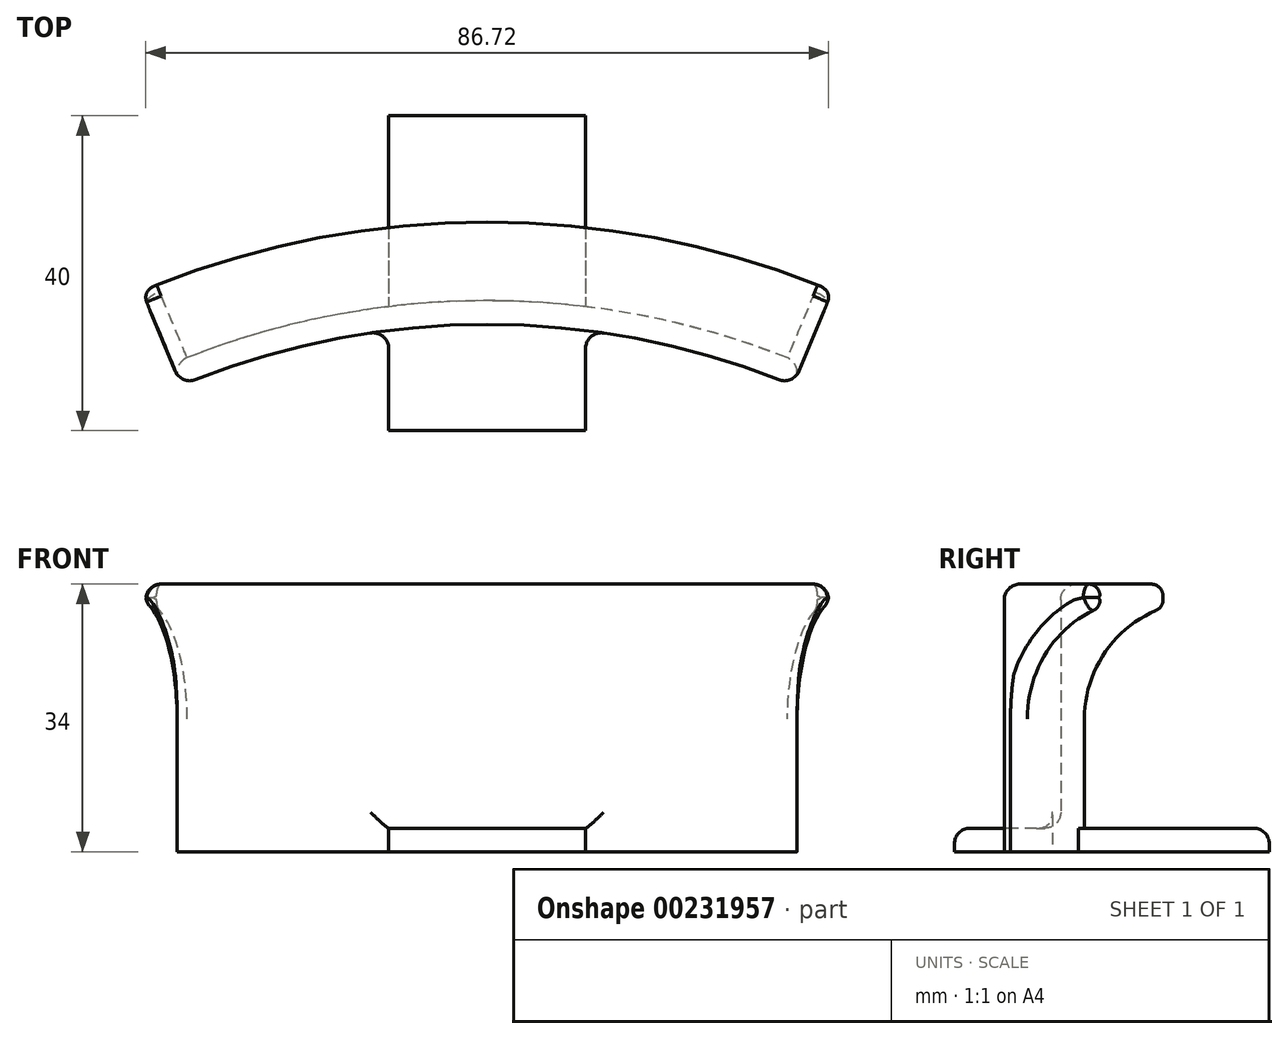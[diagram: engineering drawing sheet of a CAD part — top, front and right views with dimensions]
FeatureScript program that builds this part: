
annotation { "Feature Type Name" : "Feature", "Feature Type Description" : "" }
export const myFeature = defineFeature(function(context is Context, id is Id, definition is map)
    precondition{}
    {
        {
            var Q0;
            Q0=qCreatedBy(makeId("Top.planeOp"),FACE);
            var sketch = newSketch(context, id + "F0", { "sketchPlane" : qUnion([Q0])});
            skArc(sketch, "E0", {"start": v(40, 0) * mm, "mid": v(0, 8) * mm, "end": v(-40, 0) * mm});
            skPoint(sketch, "E1", {"position": v(0, 8) * mm});
            skArc(sketch, "E2.0", {"start": v(38.85, -2.77) * mm, "mid": v(0, 5) * mm, "end": v(-38.85, -2.77) * mm});
            skLineSegment(sketch, "E3", {"start": v(-40, 0) * mm, "end": v(-38.85, -2.77) * mm});
            skLineSegment(sketch, "E4", {"start": v(40, 0) * mm, "end": v(38.85, -2.77) * mm});
            skSolve(sketch);
        }
        {
            var Q0;
            Q0=qSketchRegion(id+"F0",true);
            var Q1;
            Q1 = qSketchRegion(id + "F2", true);
            extrude(context, id + "F1", {"entities" : qUnion([Q0, Q1]), "endBound" : BoundingType.SYMMETRIC, "depth" : 34 * mm, "hasSecondDirection" : true, "secondDirectionOppositeDirection" : true, "secondDirectionDepth" : 25 * mm});
        }
        {
            var Q0;
            Q0=makeQuery(id+"F1.opExtrude","CAP_FACE",FACE,{"disambiguationData":[OSD([sQuery(id+"F0.wireOp",EDGE,"E0"),sQuery(id+"F0.wireOp",EDGE,"E2.0"),sQuery(id+"F0.wireOp",EDGE,"E3"),sQuery(id+"F0.wireOp",EDGE,"E4"),sQuery(id+"F0.wireOp",EDGE,"MKCCxzGF-fzHT-6NQb-3Dkm-oyMVu23sNnWI"),sQuery(id+"F0.wireOp",EDGE,"RX4jBwC5-T415-0Oy0-ZdqJ-OYdbBSf1K6n9"),sQuery(id+"F0.wireOp",EDGE,"Lq5RhwRJ-kZL3-UkZd-qRQH-dxPEWorBv0Qx"),sQuery(id+"F0.wireOp",EDGE,"eGbxxHlE-VtXz-Rjba-jT0Z-kXdZI8RM2eGt"),sQuery(id+"F0.wireOp",EDGE,"FihKfQdN-VEdl-hHsK-2V6z-z5lvR1BBxPRn"),sQuery(id+"F0.wireOp",EDGE,"HknWR3fc-V9o8-nyJb-E4uW-t3jdVaxvh762"),sQuery(id+"F0.wireOp",EDGE,"368abe3e-c0fb-4884-afcf-caa45f78abb90.MirrorCS"),sQuery(id+"F0.wireOp",EDGE,"368abe3e-c0fb-4884-afcf-caa45f78abb91.MirrorCS"),sQuery(id+"F0.wireOp",EDGE,"368abe3e-c0fb-4884-afcf-caa45f78abb92.MirrorCS"),sQuery(id+"F0.wireOp",EDGE,"368abe3e-c0fb-4884-afcf-caa45f78abb93.MirrorCS"),sQuery(id+"F0.wireOp",EDGE,"368abe3e-c0fb-4884-afcf-caa45f78abb94.MirrorCS")])],"isStart":false});
            var sketch = newSketch(context, id + "F2", { "sketchPlane" : qUnion([Q0])});
            skArc(sketch, "E5", {"start": v(38.85, -2.77) * mm, "mid": v(0, 5) * mm, "end": v(-38.85, -2.77) * mm});
            skArc(sketch, "E6.0", {"start": v(43.85, 9.23) * mm, "mid": v(0, 18) * mm, "end": v(-43.85, 9.23) * mm});
            skLineSegment(sketch, "E7", {"start": v(-43.85, 9.23) * mm, "end": v(-38.85, -2.77) * mm});
            skLineSegment(sketch, "E8", {"start": v(43.85, 9.23) * mm, "end": v(38.85, -2.77) * mm});
            skSolve(sketch);
        }
        {
            var Q0;
            Q0=qSketchRegion(id+"F2",true);
            extrude(context, id + "F3", {"entities" : qUnion([Q0]), "operationType" : NewBodyOperationType.ADD, "oppositeDirection" : true, "depth" : 3 * mm});
        }
        {
            var Q0;
            Q0=makeQuery(id+"F3.boolean.opBoolean","INTERSECT",EDGE,{"derivedFrom":[makeQuery(id+"F1.opExtrude","SWEPT_FACE",FACE,{"disambiguationData":[OSD([sQuery(id+"F0.wireOp",EDGE,"E0")])]}),makeQuery(id+"F3.opExtrude","CAP_FACE",FACE,{"disambiguationData":[OSD([sQuery(id+"F2.wireOp",EDGE,"E5"),sQuery(id+"F2.wireOp",EDGE,"E6.0"),sQuery(id+"F2.wireOp",EDGE,"E7"),sQuery(id+"F2.wireOp",EDGE,"E8")])],"isStart":false})]});
            var Q1;
            Q1=makeQuery(id+"FpLEZJu2neVifi9_1.1.F3.boolean.opBoolean","INTERSECT",EDGE,{"derivedFrom":[makeQuery(id+"F1.opExtrude","SWEPT_FACE",FACE,{"disambiguationData":[OSD([sQuery(id+"F0.wireOp",EDGE,"E0")])]}),makeQuery(id+"FpLEZJu2neVifi9_1.1.F3.opExtrude","CAP_FACE",FACE,{"disambiguationData":[OSD([sQuery(id+"F2.wireOp",EDGE,"E5"),sQuery(id+"F2.wireOp",EDGE,"E6.0"),sQuery(id+"F2.wireOp",EDGE,"E7"),sQuery(id+"F2.wireOp",EDGE,"E8")])],"isStart":false})]});
            fillet(context, id + "F4", {"entities" : qUnion([Q0, Q1]), "radius" : 15 * mm, "tangentPropagation" : true, "allowEdgeOverflow" : false});
        }
        {
            var Q0;
            Q0=makeQuery(id+"FpLEZJu2neVifi9_1.1.F3.boolean.opBoolean","MERGE",FACE,{"derivedFrom":[makeQuery(id+"F1.opExtrude","CAP_FACE",FACE,{"disambiguationData":[OSD([sQuery(id+"F0.wireOp",EDGE,"E0"),sQuery(id+"F0.wireOp",EDGE,"E2.0"),sQuery(id+"F0.wireOp",EDGE,"E3"),sQuery(id+"F0.wireOp",EDGE,"E4")])],"isStart":true}),makeQuery(id+"FpLEZJu2neVifi9_1.1.F3.opExtrude","CAP_FACE",FACE,{"disambiguationData":[OSD([sQuery(id+"F2.wireOp",EDGE,"E5"),sQuery(id+"F2.wireOp",EDGE,"E6.0"),sQuery(id+"F2.wireOp",EDGE,"E7"),sQuery(id+"F2.wireOp",EDGE,"E8")])],"isStart":true})]});
            var sketch = newSketch(context, id + "F5", { "sketchPlane" : qUnion([Q0])});
            skLineSegment(sketch, "E9.bottom", {"start": v(12.5, -31.5) * mm, "end": v(-12.5, -31.5) * mm});
            skLineSegment(sketch, "E9.top", {"start": v(12.5, 8.5) * mm, "end": v(-12.5, 8.5) * mm});
            skLineSegment(sketch, "E9.left", {"start": v(12.5, -31.5) * mm, "end": v(12.5, 8.5) * mm});
            skLineSegment(sketch, "E9.right", {"start": v(-12.5, -31.5) * mm, "end": v(-12.5, 8.5) * mm});
            skLineSegment(sketch, "E10", {"start": v(0, -18) * mm, "end": v(0, -5) * mm, "construction": true});
            skPoint(sketch, "E11", {"position": v(0, -11.5) * mm});
            skLineSegment(sketch, "E12", {"start": v(12.5, -31.5) * mm, "end": v(-12.5, 8.5) * mm, "construction": true});
            skSolve(sketch);
        }
        {
            var Q0;
            Q0 = qSketchRegion(id + "F5", true);
            extrude(context, id + "F6", {"entities" : qUnion([Q0]), "operationType" : NewBodyOperationType.ADD, "oppositeDirection" : true, "depth" : 3 * mm});
        }
        {
            var Q0;
            Q0=makeQuery(id+"F6.boolean.opBoolean","INTERSECT",EDGE,{"derivedFrom":[makeQuery(id+"FpLEZJu2neVifi9_1.1.F3.opExtrude","SWEPT_FACE",FACE,{"disambiguationData":[OSD([sQuery(id+"F2.wireOp",EDGE,"E6.0")])]}),makeQuery(id+"F6.opExtrude","SWEPT_FACE",FACE,{"disambiguationData":[OSD([sQuery(id+"F5.wireOp",EDGE,"E9.left")])]})]});
            var Q1;
            Q1=makeQuery(id+"F6.boolean.opBoolean","INTERSECT",EDGE,{"derivedFrom":[makeQuery(id+"FpLEZJu2neVifi9_1.1.F3.opExtrude","SWEPT_FACE",FACE,{"disambiguationData":[OSD([sQuery(id+"F2.wireOp",EDGE,"E6.0")])]}),makeQuery(id+"F6.opExtrude","SWEPT_FACE",FACE,{"disambiguationData":[OSD([sQuery(id+"F5.wireOp",EDGE,"E9.right")])]})]});
            var Q2;
            Q2=makeQuery(id+"F6.boolean.opBoolean","INTERSECT",EDGE,{"derivedFrom":[makeQuery(id+"F1.opExtrude","SWEPT_FACE",FACE,{"disambiguationData":[OSD([sQuery(id+"F0.wireOp",EDGE,"E2.0")])]}),makeQuery(id+"F6.opExtrude","SWEPT_FACE",FACE,{"disambiguationData":[OSD([sQuery(id+"F5.wireOp",EDGE,"E9.left")])]})]});
            var Q3;
            Q3=makeQuery(id+"F6.boolean.opBoolean","INTERSECT",EDGE,{"derivedFrom":[makeQuery(id+"F1.opExtrude","SWEPT_FACE",FACE,{"disambiguationData":[OSD([sQuery(id+"F0.wireOp",EDGE,"E2.0")])]}),makeQuery(id+"F6.opExtrude","SWEPT_FACE",FACE,{"disambiguationData":[OSD([sQuery(id+"F5.wireOp",EDGE,"E9.right")])]})]});
            var Q4;
            {var subQ0=sQuery(id+"F2.wireOp",EDGE,"E7");Q4=makeQuery(id+"FpLEZJu2neVifi9_1.1.F3.boolean.opBoolean","MERGE",FACE,{"derivedFrom":[makeQuery(id+"F3.boolean.opBoolean","MERGE",FACE,{"derivedFrom":[makeQuery(id+"F1.opExtrude","SWEPT_FACE",FACE,{"disambiguationData":[OSD([sQuery(id+"F0.wireOp",EDGE,"E3")])]}),makeQuery(id+"F3.opExtrude","SWEPT_FACE",FACE,{"disambiguationData":[OSD([subQ0])]})]}),makeQuery(id+"FpLEZJu2neVifi9_1.1.F3.opExtrude","SWEPT_FACE",FACE,{"disambiguationData":[OSD([subQ0])]})]});}
            var Q5;
            {var subQ0=sQuery(id+"F2.wireOp",EDGE,"E8");Q5=makeQuery(id+"FpLEZJu2neVifi9_1.1.F3.boolean.opBoolean","MERGE",FACE,{"derivedFrom":[makeQuery(id+"F3.boolean.opBoolean","MERGE",FACE,{"derivedFrom":[makeQuery(id+"F1.opExtrude","SWEPT_FACE",FACE,{"disambiguationData":[OSD([sQuery(id+"F0.wireOp",EDGE,"E4")])]}),makeQuery(id+"F3.opExtrude","SWEPT_FACE",FACE,{"disambiguationData":[OSD([subQ0])]})]}),makeQuery(id+"FpLEZJu2neVifi9_1.1.F3.opExtrude","SWEPT_FACE",FACE,{"disambiguationData":[OSD([subQ0])]})]});}
            var Q6;
            Q6=makeQuery(id+"F1.opExtrude","CAP_EDGE",EDGE,{"disambiguationData":[OSD([sQuery(id+"F0.wireOp",EDGE,"E2.0")])],"isStart":false});
            var Q7;
            Q7=makeQuery(id+"F6.opExtrude","CAP_EDGE",EDGE,{"disambiguationData":[OSD([sQuery(id+"F5.wireOp",EDGE,"E9.bottom")])],"isStart":false});
            var Q8;
            Q8=makeQuery(id+"F6.opExtrude","CAP_EDGE",EDGE,{"disambiguationData":[OSD([sQuery(id+"F5.wireOp",EDGE,"E9.top")])],"isStart":false});
            var Q9;
            Q9=makeQuery(id+"F6.boolean.opBoolean","INTERSECT",EDGE,{"derivedFrom":[makeQuery(id+"F1.opExtrude","SWEPT_FACE",FACE,{"disambiguationData":[OSD([sQuery(id+"F0.wireOp",EDGE,"E2.0")])]}),makeQuery(id+"F6.opExtrude","CAP_FACE",FACE,{"disambiguationData":[OSD([sQuery(id+"F5.wireOp",EDGE,"E9.bottom"),sQuery(id+"F5.wireOp",EDGE,"E9.top"),sQuery(id+"F5.wireOp",EDGE,"E9.left"),sQuery(id+"F5.wireOp",EDGE,"E9.right")])],"isStart":false})]});
            fillet(context, id + "F7", {"entities" : qUnion([Q0, Q1, Q2, Q3, Q4, Q5, Q6, Q7, Q8, Q9]), "radius" : 2 * mm, "tangentPropagation" : true, "allowEdgeOverflow" : false});
        }
        {
            var Q0;
            Q0=makeQuery(id+"F3.opExtrude","SWEPT_FACE",FACE,{"disambiguationData":[OSD([sQuery(id+"F2.wireOp",EDGE,"E6.0")])]});
            fillet(context, id + "F8", {"entities" : qUnion([Q0]), "radius" : 1.5 * mm, "tangentPropagation" : true, "allowEdgeOverflow" : false});
        }
    });
